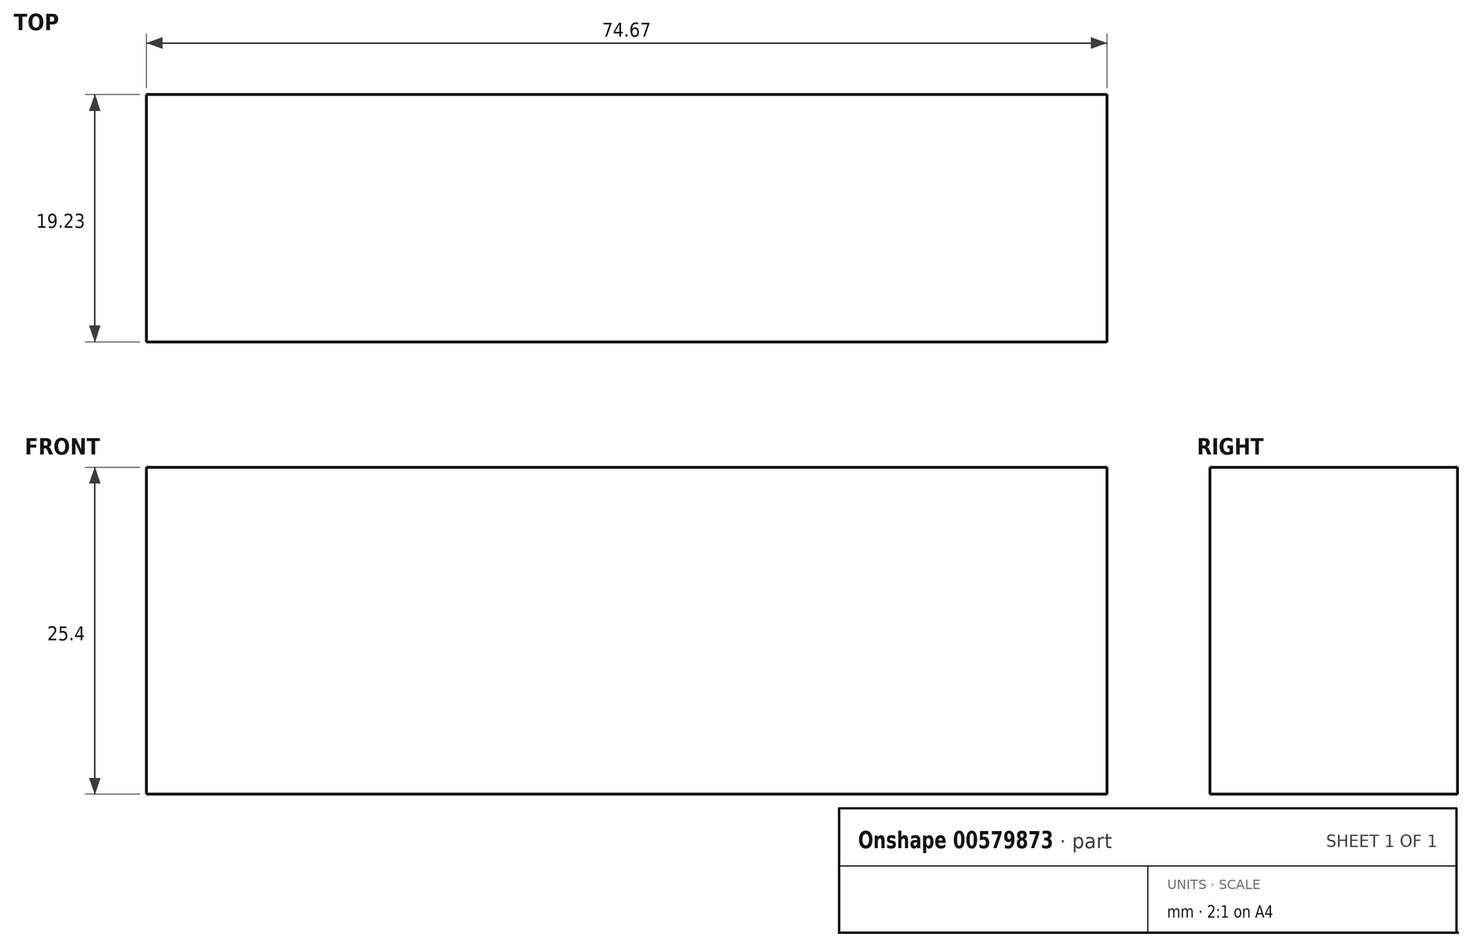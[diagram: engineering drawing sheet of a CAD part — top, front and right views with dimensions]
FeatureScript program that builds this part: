
annotation { "Feature Type Name" : "Feature", "Feature Type Description" : "" }
export const myFeature = defineFeature(function(context is Context, id is Id, definition is map)
    precondition{}
    {
        {
            var Q0;
            Q0=qCreatedBy(makeId("Top.planeOp"),FACE);
            var sketch = newSketch(context, id + "F0", { "sketchPlane" : qUnion([Q0])});
            skLineSegment(sketch, "E0.bottom", {"start": v(-48.96, 0) * mm, "end": v(25.7, 0) * mm});
            skLineSegment(sketch, "E0.top", {"start": v(-48.96, -19.23) * mm, "end": v(25.7, -19.23) * mm});
            skLineSegment(sketch, "E0.left", {"start": v(-48.96, 0) * mm, "end": v(-48.96, -19.23) * mm});
            skLineSegment(sketch, "E0.right", {"start": v(25.7, 0) * mm, "end": v(25.7, -19.23) * mm});
            skSolve(sketch);
        }
        {
            var Q0;
            Q0=makeQuery(id+"F0.imprint","IMPRINT",FACE,{"disambiguationData":[TD([[makeQuery(id+"F0.imprint","IMPRINT",EDGE,{"derivedFrom":sQuery(id+"F0.wireOp",EDGE,"E0.bottom")}),-1.0]])]});
            extrude(context, id + "F1", {"entities" : qUnion([Q0]), "depth" : 25.4 * mm, "offsetDistance" : 25.4 * mm});
        }
    });
